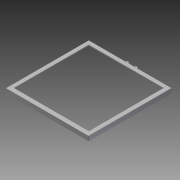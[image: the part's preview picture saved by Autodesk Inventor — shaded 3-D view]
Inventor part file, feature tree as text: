
AUTODESK INVENTOR PART (.ipt)
format: ipt  version: 2013 SP2 (Build 170200200, 200)  size: 183,808 bytes
history: native  units: in
note: dims shown in document units (in); Inventor stores cm internally (conversion verified against a paired STEP export)
features: extrude x6, sketch x6, fillet x3, mirror x3, thread x2
ambient origin geometry x8: Origin, YZ Plane, XZ Plane, XY Plane, X Axis, Y Axis, Z Axis, Center Point
bodies: Solid1 (feature_tree)
feature tree (20):
  extrude  "Extrusion1"  Depth=25.997in
  extrude  "Extrusion2"  Depth=0.0625in
  fillet  "Fillet1"  Radius=1.4375in
  extrude  "Extrusion3"  Depth=0.125in
  extrude  "Extrusion4"  Depth=0.375in
  fillet  "Fillet2"  Radius=0.75in
  fillet  "Fillet3"  Radius=0.75in
  mirror  "Mirror1"
  extrude  "Extrusion5"  Depth=0.375in
  thread  "Thread1"  [1 undecoded]
  mirror  "Mirror2"
  thread  "Thread2"  [1 undecoded]
  extrude  "Extrusion6"  Depth=0.0625in
  mirror  "Mirror3"
  sketch  "Sketch1"  dims[d0=25.997in d2=25.997in]
  sketch  "Sketch2"  dims[d3=0.0625in d4=0.0625in d5=1.4375in d6=0.0in]
  sketch  "Sketch3"  dims[d9=0.0625in d10=0.0in d11=0.125in]
  sketch  "Sketch4"  dims[d12=0.75in d14=0.375in d15=0.75in d17=0.75in d18=0.0in]
  sketch  "Sketch5"  dims[d19=0.25in d21=0.375in d22=0.375in d23=0.75in d24=0.0in]
  sketch  "Sketch6"  dims[d25=0.0625in d26=0.0625in d27=0.25in d28=0.3125in d29=0.3125in d30=0.75in d31=0.0in d32=1.0in d33=0.0in d34=1.0in d35=0.0in d36=0.25in d37=2.375in d38=0.75in d39=0.0in d142=-2.3125in d145=1.0in d146=1.25in d147=1.25in]
note: 2 required parameter values undecoded (feature->parameter linkage not recoverable at this tier; creation-order binding heuristic only, values carry confidence <= 0.55)
